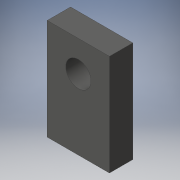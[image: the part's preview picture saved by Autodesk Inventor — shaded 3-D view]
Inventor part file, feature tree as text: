
AUTODESK INVENTOR PART (.ipt)
format: ipt  version: 2016 (Build 200138000, 138)  size: 111,616 bytes
history: native  units: in
note: dims shown in document units (in); Inventor stores cm internally (conversion verified against a paired STEP export)
features: extrude x3, sketch x3
ambient origin geometry x8: Origin, YZ Plane, XZ Plane, XY Plane, X Axis, Y Axis, Z Axis, Center Point
bodies: Solid1 (feature_tree)
feature tree (6):
  extrude  "Extrusion1"  Depth=0.5906in
  extrude  "Extrusion2"  Depth=0.7874in
  extrude  "Extrusion3"  Depth=0.5394in TaperAngle=0.0deg
  sketch  "Sketch1"  dims[d0=1.5748in d1=0.5906in]
  sketch  "Sketch2"  dims[d2=0.2953in d3=0.7874in]
  sketch  "Sketch3"  dims[d4=2.5591in d5=0.0in d10=0.5394in d11=0.0in d12=1.7795in d13=0.6398in d14=0.7874in d15=0.0in d21=0.0197in d22=0.315in d23=0.315in d24=0.1516in d25=0.1516in]
